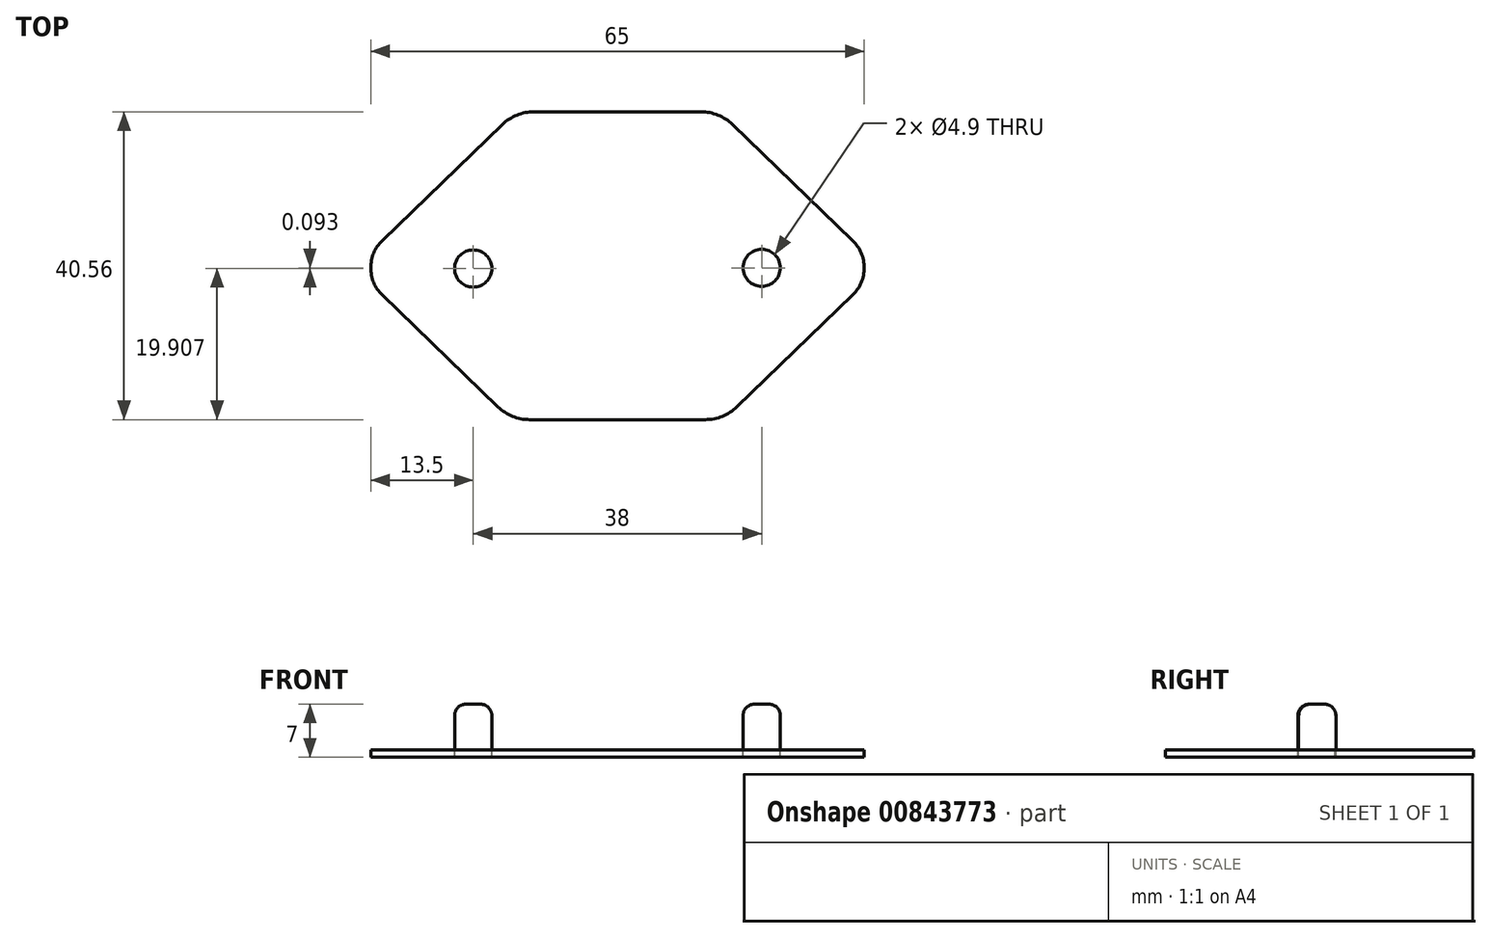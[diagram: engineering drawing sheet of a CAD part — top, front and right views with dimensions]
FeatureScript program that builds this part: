
annotation { "Feature Type Name" : "Feature", "Feature Type Description" : "" }
export const myFeature = defineFeature(function(context is Context, id is Id, definition is map)
    precondition{}
    {
        {
            var Q0;
            Q0=qCreatedBy(makeId("Top.planeOp"),FACE);
            var sketch = newSketch(context, id + "F0", { "sketchPlane" : qUnion([Q0])});
            skLineSegment(sketch, "E0.bottom", {"start": v(-11, 20.56) * mm, "end": v(0, 20.56) * mm});
            skLineSegment(sketch, "E0.top", {"start": v(-11.57, -20) * mm, "end": v(0, -20) * mm});
            skPoint(sketch, "E0.middle", {"position": v(0, 0) * mm});
            skLineSegment(sketch, "E1", {"start": v(-30.97, 3.6) * mm, "end": v(-15.16, 18.88) * mm});
            skLineSegment(sketch, "E2", {"start": v(-30.97, -3.6) * mm, "end": v(-15.74, -18.31) * mm});
            skPoint(sketch, "E3.startSnap0", {"position": v(-22.2, 12.08) * mm});
            skArc(sketch, "E4", {"start": v(-30.97, 3.6) * mm, "mid": v(-32.5, 0) * mm, "end": v(-30.97, -3.6) * mm});
            skLineSegment(sketch, "E5", {"start": v(0, 20.56) * mm, "end": v(0, -20) * mm});
            skPoint(sketch, "E6.visualSharp", {"position": v(-13.42, 20.56) * mm});
            skArc(sketch, "E6.filletArc", {"start": v(-11, 20.56) * mm, "mid": v(-13.24, 20.12) * mm, "end": v(-15.16, 18.88) * mm});
            skPoint(sketch, "E7.visualSharp", {"position": v(-14, -20) * mm});
            skArc(sketch, "E7.filletArc", {"start": v(-15.74, -18.31) * mm, "mid": v(-13.82, -19.56) * mm, "end": v(-11.57, -20) * mm});
            skArc(sketch, "E8.MirrorCS", {"start": v(15.74, -18.31) * mm, "mid": v(13.82, -19.56) * mm, "end": v(11.57, -20) * mm});
            skArc(sketch, "E9.MirrorCS", {"start": v(11, 20.56) * mm, "mid": v(13.24, 20.12) * mm, "end": v(15.16, 18.88) * mm});
            skLineSegment(sketch, "E10.MirrorCS", {"start": v(11.57, -20) * mm, "end": v(0, -20) * mm});
            skLineSegment(sketch, "E11.MirrorCS", {"start": v(11, 20.56) * mm, "end": v(0, 20.56) * mm});
            skPoint(sketch, "E12.MirrorP", {"position": v(14, -20) * mm});
            skPoint(sketch, "E13.MirrorP", {"position": v(13.42, 20.56) * mm});
            skLineSegment(sketch, "E14.MirrorCS", {"start": v(30.97, 3.6) * mm, "end": v(15.16, 18.88) * mm});
            skArc(sketch, "E15.MirrorCS", {"start": v(30.97, 3.6) * mm, "mid": v(32.5, 0) * mm, "end": v(30.97, -3.6) * mm});
            skPoint(sketch, "E16.MirrorP", {"position": v(22.2, 12.08) * mm});
            skLineSegment(sketch, "E17.MirrorCS", {"start": v(30.97, -3.6) * mm, "end": v(15.74, -18.31) * mm});
            skCircle(sketch, "E18", {"center": v(-19, -0.1) * mm, "radius": 2.45 * mm});
            skCircle(sketch, "E19", {"center": v(19, 0) * mm, "radius": 2.45 * mm});
            skSolve(sketch);
        }
        {
            var Q0;
            Q0=makeQuery(id+"F0.imprint","IMPRINT",FACE,{"disambiguationData":[TD([[makeQuery(id+"F0.imprint","IMPRINT",EDGE,{"derivedFrom":sQuery(id+"F0.wireOp",EDGE,"E5")}),1.0]])]});
            var Q1;
            Q1=makeQuery(id+"F0.imprint","IMPRINT",FACE,{"disambiguationData":[TD([[makeQuery(id+"F0.imprint","IMPRINT",EDGE,{"derivedFrom":sQuery(id+"F0.wireOp",EDGE,"E0.bottom")}),-1.0]])]});
            var Q2;
            Q2=makeQuery(id+"F0.imprint","IMPRINT",FACE,{"disambiguationData":[TD([[makeQuery(id+"F0.imprint","IMPRINT",EDGE,{"derivedFrom":sQuery(id+"F0.wireOp",EDGE,"ef57985a-5634-45e9-8a15-d269099bb73b6.MirrorC")}),-1.0]])]});
            var Q3;
            Q3=makeQuery(id+"F0.imprint","IMPRINT",FACE,{"disambiguationData":[TD([[makeQuery(id+"F0.imprint","IMPRINT",EDGE,{"derivedFrom":sQuery(id+"F0.wireOp",EDGE,"kWgewc3X-PaKK-i7qB-fbcE-h9dMDVYHUhFD")}),1.0]])]});
            var Q4;
            Q4=makeQuery(id+"F0.imprint","IMPRINT",FACE,{"disambiguationData":[TD([[makeQuery(id+"F0.imprint","IMPRINT",EDGE,{"derivedFrom":sQuery(id+"F0.wireOp",EDGE,"ef57985a-5634-45e9-8a15-d269099bb73b7.MirrorC")}),-1.0]])]});
            var Q5;
            Q5=makeQuery(id+"F0.imprint","IMPRINT",FACE,{"disambiguationData":[TD([[makeQuery(id+"F0.imprint","IMPRINT",EDGE,{"derivedFrom":sQuery(id+"F0.wireOp",EDGE,"uVkAt3nz-HI2k-V4Pd-sQZP-paNsz8DFQ8WT")}),1.0]])]});
            extrude(context, id + "F1", {"entities" : qUnion([Q0, Q1, Q2, Q3, Q4, Q5]), "oppositeDirection" : true, "depth" : 1 * mm, "offsetDistance" : 25 * mm});
        }
        {
            var Q0;
            Q0=makeQuery(id+"F0.imprint","IMPRINT",FACE,{"disambiguationData":[TD([[makeQuery(id+"F0.imprint","IMPRINT",EDGE,{"derivedFrom":sQuery(id+"F0.wireOp",EDGE,"E18")}),1.0]])]});
            var Q1;
            Q1=makeQuery(id+"F0.imprint","IMPRINT",FACE,{"disambiguationData":[TD([[makeQuery(id+"F0.imprint","IMPRINT",EDGE,{"derivedFrom":sQuery(id+"F0.wireOp",EDGE,"E19")}),1.0]])]});
            extrude(context, id + "F2", {"entities" : qUnion([Q0, Q1]), "depth" : 6 * mm, "offsetDistance" : 25 * mm});
        }
        {
            var Q0;
            Q0=makeQuery(id+"F2.opExtrude","CAP_EDGE",EDGE,{"disambiguationData":[OSD([sQuery(id+"F0.wireOp",EDGE,"E18")])],"isStart":false});
            fillet(context, id + "F3", {"entities" : qUnion([Q0]), "radius" : 1.5 * mm, "tangentPropagation" : true, "allowEdgeOverflow" : false});
        }
        {
            var Q0;
            Q0=makeQuery(id+"F2.opExtrude","CAP_EDGE",EDGE,{"disambiguationData":[OSD([sQuery(id+"F0.wireOp",EDGE,"E19")])],"isStart":false});
            fillet(context, id + "F4", {"entities" : qUnion([Q0]), "radius" : 1.5 * mm, "tangentPropagation" : true, "allowEdgeOverflow" : false});
        }
        {
            var Q0;
            Q0=makeQuery(id+"F2.opExtrude","CAP_FACE",FACE,{"disambiguationData":[OSD([sQuery(id+"F0.wireOp",EDGE,"E19")])],"isStart":true});
            var Q1;
            Q1=makeQuery(id+"F2.opExtrude","CAP_FACE",FACE,{"disambiguationData":[OSD([sQuery(id+"F0.wireOp",EDGE,"E18")])],"isStart":true});
            extrude(context, id + "F5", {"entities" : qUnion([Q0, Q1]), "depth" : 1 * mm, "offsetDistance" : 25 * mm});
        }
    });
